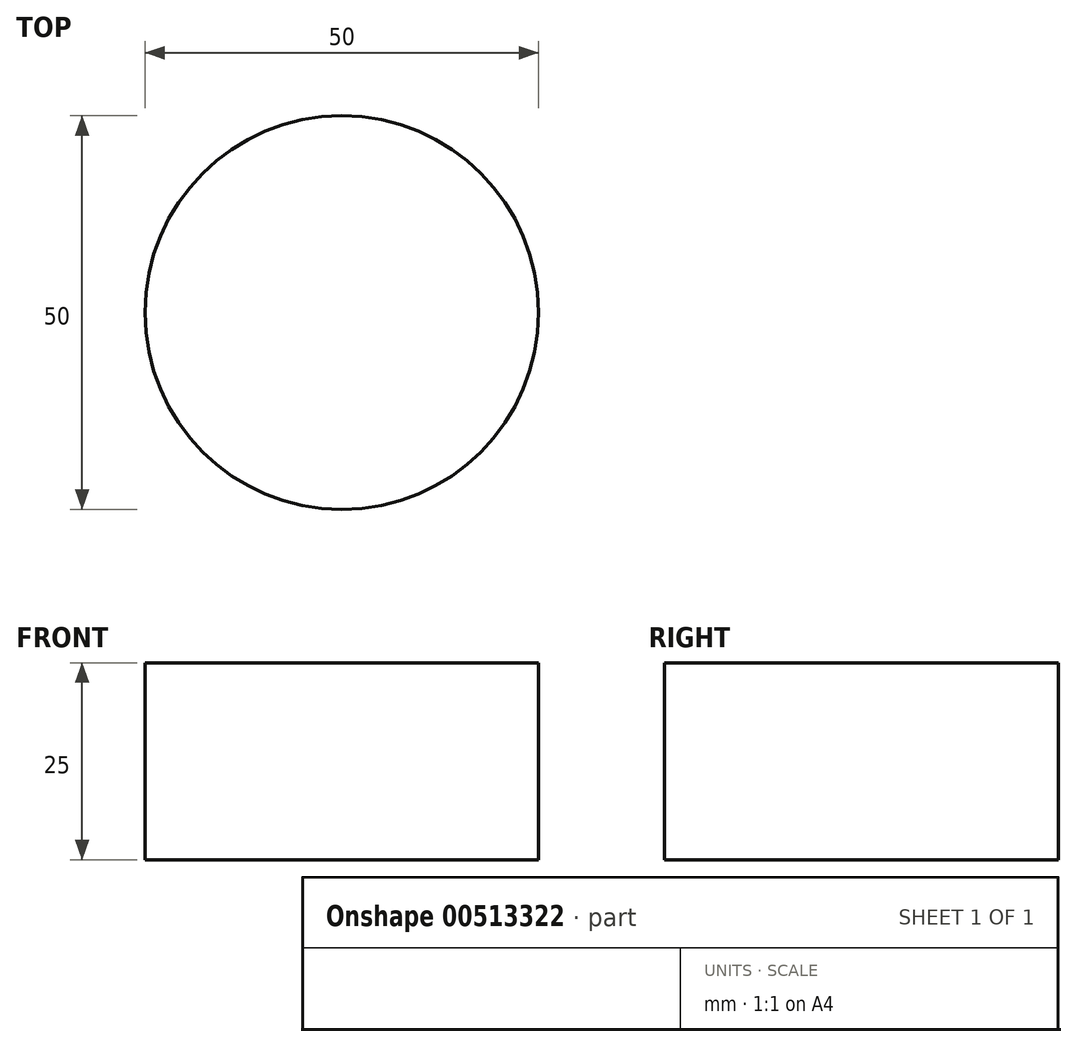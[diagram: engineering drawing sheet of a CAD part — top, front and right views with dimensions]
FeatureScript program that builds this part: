
annotation { "Feature Type Name" : "Feature", "Feature Type Description" : "" }
export const myFeature = defineFeature(function(context is Context, id is Id, definition is map)
    precondition{}
    {
        {
            var Q0;
            Q0=qCreatedBy(makeId("Top.planeOp"),FACE);
            var sketch = newSketch(context, id + "F0", { "sketchPlane" : qUnion([Q0])});
            skCircle(sketch, "E0", {"center": v(0, 0) * mm, "radius": 25 * mm});
            skSolve(sketch);
        }
        {
            var Q0;
            Q0=makeQuery(id+"F0.imprint","IMPRINT",FACE,{"disambiguationData":[TD([[makeQuery(id+"F0.imprint","IMPRINT",EDGE,{"derivedFrom":sQuery(id+"F0.wireOp",EDGE,"E0")}),1.0]])]});
            extrude(context, id + "F1", {"entities" : qUnion([Q0]), "depth" : 25 * mm});
        }
    });
